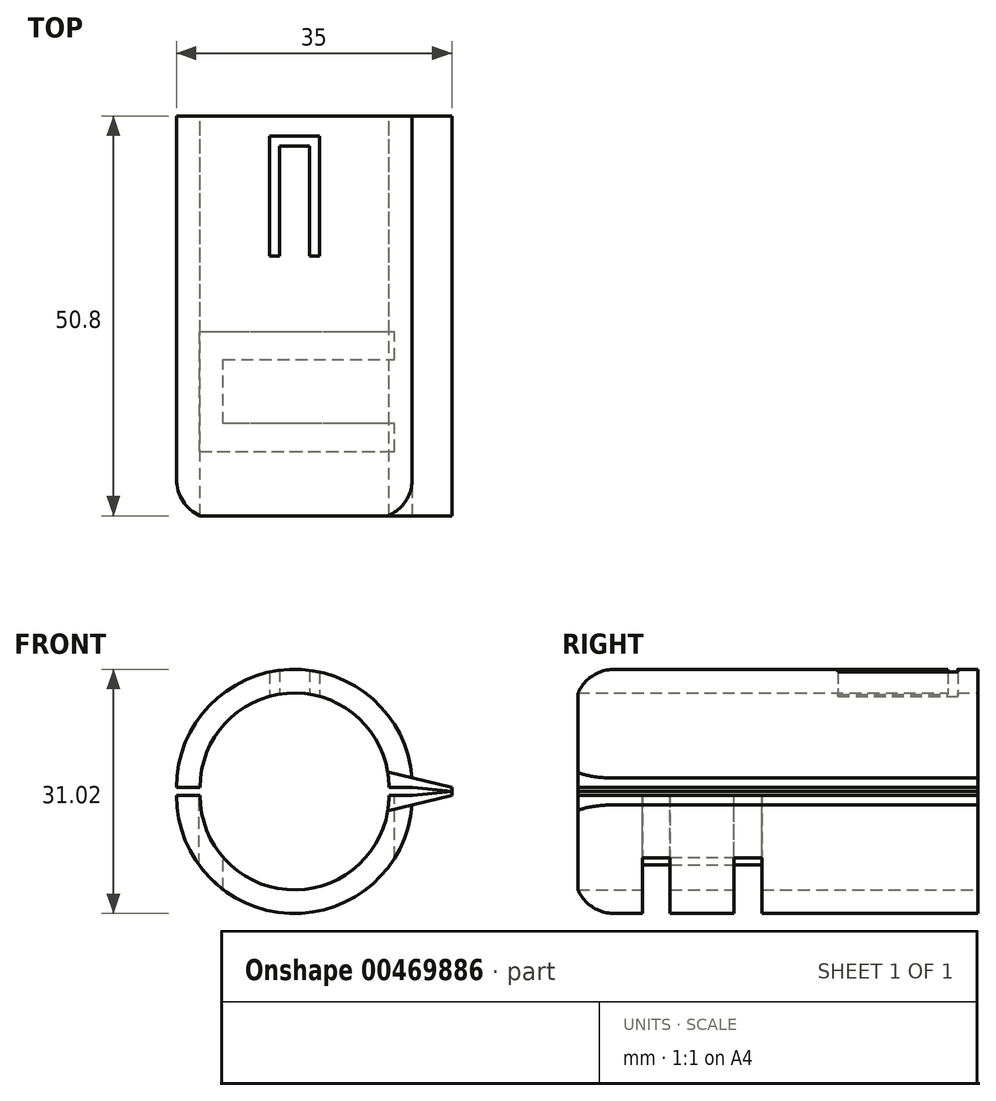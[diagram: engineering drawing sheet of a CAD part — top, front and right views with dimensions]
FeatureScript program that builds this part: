
annotation { "Feature Type Name" : "Feature", "Feature Type Description" : "" }
export const myFeature = defineFeature(function(context is Context, id is Id, definition is map)
    precondition{}
    {
        {
            var Q0;
            Q0=qCreatedBy(makeId("Front.planeOp"),FACE);
            var sketch = newSketch(context, id + "F0", { "sketchPlane" : qUnion([Q0])});
            skArc(sketch, "E0", {"start": v(15, 0) * mm, "mid": v(0, -15) * mm, "end": v(-15, 0) * mm});
            skArc(sketch, "E1", {"start": v(12, 0) * mm, "mid": v(0, -12) * mm, "end": v(-12, 0) * mm});
            skLineSegment(sketch, "E2", {"start": v(12, 0) * mm, "end": v(15, 0) * mm});
            skLineSegment(sketch, "E3", {"start": v(-12, 0) * mm, "end": v(-15, 0) * mm});
            skLineSegment(sketch, "E4", {"start": v(15, 0) * mm, "end": v(20, 0.5) * mm});
            skLineSegment(sketch, "E5", {"start": v(14.95, -1.2) * mm, "end": v(20, 0) * mm});
            skLineSegment(sketch, "E6", {"start": v(20, 0) * mm, "end": v(20, 0.5) * mm});
            skSolve(sketch);
        }
        {
            var Q0;
            Q0 = qSketchRegion(id + "F0", true);
            extrude(context, id + "F1", {"entities" : qUnion([Q0]), "depth" : 50.8 * mm});
        }
        {
            var Q0;
            Q0=makeQuery(id+"F1.opExtrude","SWEPT_FACE",FACE,{"disambiguationData":[OSD([sQuery(id+"F0.wireOp",EDGE,"E2")])]});
            var Q1;
            Q1=makeQuery(id+"F1.opExtrude","CAP_VERTEX",VERTEX,{"disambiguationData":[OSD([sQuery(id+"F0.wireOp",EDGE,"E4"),sQuery(id+"F0.wireOp",EDGE,"E6")])],"isStart":false});
            cPlane(context, id + "F2", {"entities" : qUnion([Q0, Q1]), "cplaneType" : CPlaneType.PLANE_POINT, "offset" : 25.4 * mm, "width" : 152.4 * mm, "height" : 152.4 * mm});
        }
        {
            var Q0;
            Q0=makeQuery(id+"F1.opExtrude","SWEPT_BODY",BODY,{"disambiguationData":[OSD([sQuery(id+"F0.wireOp",EDGE,"E0"),sQuery(id+"F0.wireOp",EDGE,"E1"),sQuery(id+"F0.wireOp",EDGE,"E2"),sQuery(id+"F0.wireOp",EDGE,"E3"),sQuery(id+"F0.wireOp",EDGE,"E4"),sQuery(id+"F0.wireOp",EDGE,"E5"),sQuery(id+"F0.wireOp",EDGE,"E6")])]});
            var Q1;
            Q1=qCreatedBy(id+"F2.planeOp",FACE);
            mirror(context, id + "F3", {"entities" : qUnion([Q0]), "mirrorPlane" : qUnion([Q1])});
        }
        {
            var Q0;
            Q0=qCreatedBy(makeId("Top.planeOp"),FACE);
            var sketch = newSketch(context, id + "F4", { "sketchPlane" : qUnion([Q0])});
            skLineSegment(sketch, "E7", {"start": v(-3.18, -17.78) * mm, "end": v(-3.18, -2.54) * mm});
            skLineSegment(sketch, "E8", {"start": v(-3.18, -2.54) * mm, "end": v(3.17, -2.54) * mm});
            skLineSegment(sketch, "E9", {"start": v(3.17, -2.54) * mm, "end": v(3.17, -17.78) * mm});
            skLineSegment(sketch, "E10", {"start": v(3.17, -17.78) * mm, "end": v(1.9, -17.78) * mm});
            skLineSegment(sketch, "E11", {"start": v(1.9, -17.78) * mm, "end": v(1.9, -3.81) * mm});
            skLineSegment(sketch, "E12", {"start": v(1.9, -3.81) * mm, "end": v(-1.9, -3.81) * mm});
            skLineSegment(sketch, "E13", {"start": v(-1.9, -3.81) * mm, "end": v(-1.9, -17.78) * mm});
            skLineSegment(sketch, "E14", {"start": v(-1.9, -17.78) * mm, "end": v(-3.18, -17.78) * mm});
            skSolve(sketch);
        }
        {
            var Q0;
            Q0 = qSketchRegion(id + "F4", true);
            extrude(context, id + "F5", {"entities" : qUnion([Q0]), "operationType" : NewBodyOperationType.REMOVE, "endBound" : BoundingType.THROUGH_ALL, "depth" : 25.4 * mm});
        }
        {
            var Q0;
            Q0=qCreatedBy(makeId("Top.planeOp"),FACE);
            var sketch = newSketch(context, id + "F6", { "sketchPlane" : qUnion([Q0])});
            skLineSegment(sketch, "E15", {"start": v(12.72, -27.43) * mm, "end": v(-12.11, -27.43) * mm});
            skLineSegment(sketch, "E16", {"start": v(-12.11, -27.43) * mm, "end": v(-12.11, -42.62) * mm});
            skLineSegment(sketch, "E17", {"start": v(-12.11, -42.62) * mm, "end": v(12.72, -42.62) * mm});
            skLineSegment(sketch, "E18", {"start": v(12.72, -42.62) * mm, "end": v(12.72, -39.1) * mm});
            skLineSegment(sketch, "E19", {"start": v(12.72, -39.1) * mm, "end": v(-9.04, -39.1) * mm});
            skLineSegment(sketch, "E20", {"start": v(-9.04, -39.1) * mm, "end": v(-9.04, -30.95) * mm});
            skLineSegment(sketch, "E21", {"start": v(-9.04, -30.95) * mm, "end": v(12.72, -30.95) * mm});
            skLineSegment(sketch, "E22", {"start": v(12.72, -30.95) * mm, "end": v(12.72, -27.43) * mm});
            skSolve(sketch);
        }
        {
            var Q0;
            Q0 = qSketchRegion(id + "F6", true);
            extrude(context, id + "F7", {"entities" : qUnion([Q0]), "operationType" : NewBodyOperationType.REMOVE, "oppositeDirection" : true, "depth" : 25.4 * mm});
        }
        {
            var Q0;
            Q0=makeQuery(id+"F3.opPattern","COPY",EDGE,{"derivedFrom":makeQuery(id+"F1.opExtrude","CAP_EDGE",EDGE,{"disambiguationData":[OSD([sQuery(id+"F0.wireOp",EDGE,"E0")])],"isStart":false}),"instanceName":"1"});
            var Q1;
            Q1=makeQuery(id+"F1.opExtrude","CAP_EDGE",EDGE,{"disambiguationData":[OSD([sQuery(id+"F0.wireOp",EDGE,"E0")])],"isStart":false});
            fillet(context, id + "F8", {"entities" : qUnion([Q0, Q1]), "radius" : 5.08 * mm, "tangentPropagation" : true, "allowEdgeOverflow" : false});
        }
    });
